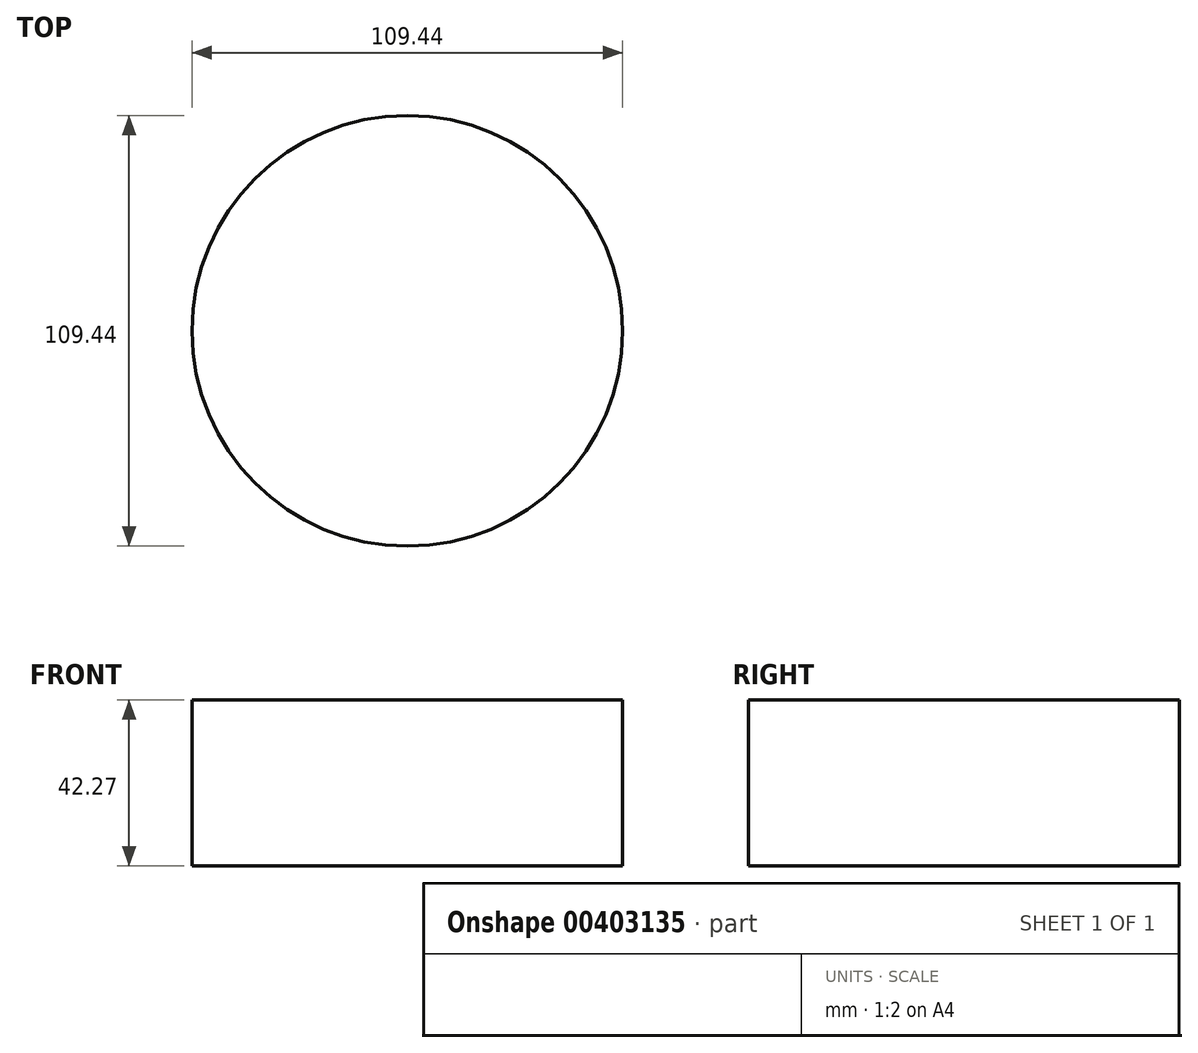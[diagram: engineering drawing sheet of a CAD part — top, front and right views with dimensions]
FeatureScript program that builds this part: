
annotation { "Feature Type Name" : "Feature", "Feature Type Description" : "" }
export const myFeature = defineFeature(function(context is Context, id is Id, definition is map)
    precondition{}
    {
        {
            var Q0;
            Q0=qCreatedBy(makeId("Top.planeOp"),FACE);
            var sketch = newSketch(context, id + "F0", { "sketchPlane" : qUnion([Q0])});
            skCircle(sketch, "E0", {"center": v(0, 0) * mm, "radius": 54.72 * mm});
            skSolve(sketch);
        }
        {
            var Q0;
            Q0 = qSketchRegion(id + "F0", true);
            extrude(context, id + "F1", {"entities" : qUnion([Q0]), "depth" : 42.27 * mm});
        }
    });
